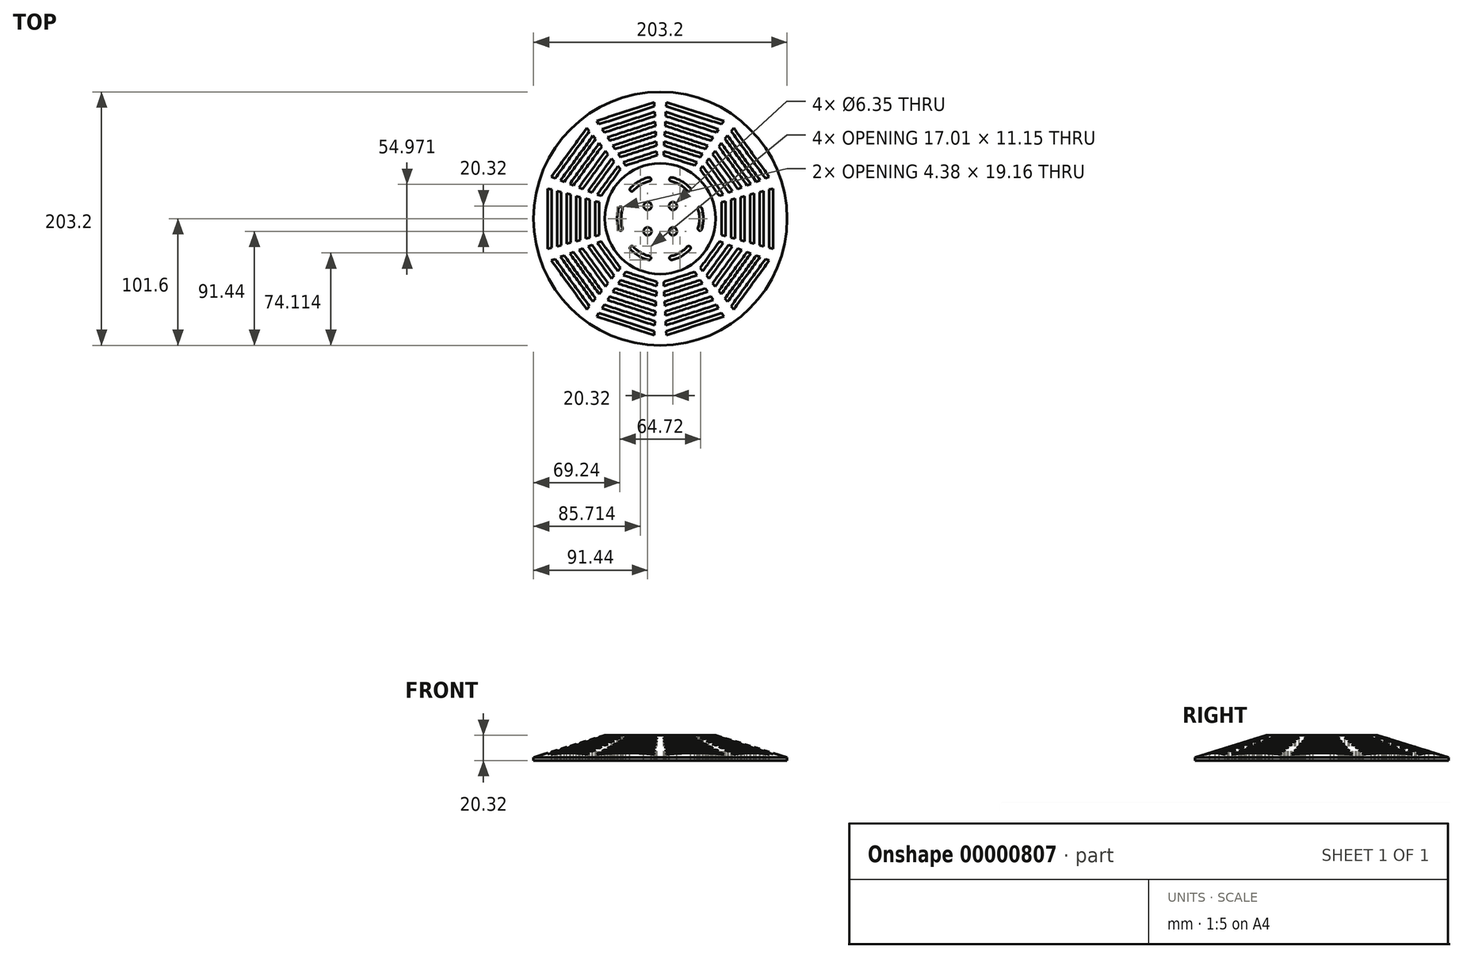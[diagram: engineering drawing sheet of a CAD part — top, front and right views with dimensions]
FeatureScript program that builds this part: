
annotation { "Feature Type Name" : "Feature", "Feature Type Description" : "" }
export const myFeature = defineFeature(function(context is Context, id is Id, definition is map)
    precondition{}
    {
        {
            var Q0;
            Q0=qCreatedBy(makeId("Front.planeOp"),FACE);
            var sketch = newSketch(context, id + "F0", { "sketchPlane" : qUnion([Q0])});
            skLineSegment(sketch, "E0", {"start": v(0, 0) * mm, "end": v(0, 20.32) * mm});
            skLineSegment(sketch, "E1", {"start": v(0, 20.32) * mm, "end": v(44.45, 20.32) * mm});
            skLineSegment(sketch, "E2", {"start": v(44.45, 20.32) * mm, "end": v(101.6, 2.54) * mm});
            skLineSegment(sketch, "E3", {"start": v(101.6, 2.54) * mm, "end": v(101.6, 0) * mm});
            skLineSegment(sketch, "E4", {"start": v(101.6, 0) * mm, "end": v(0, 0) * mm});
            skSolve(sketch);
        }
        {
            var Q0;
            Q0=makeQuery(id+"F0.imprint","IMPRINT",FACE,{"disambiguationData":[TD([[makeQuery(id+"F0.imprint","IMPRINT",EDGE,{"derivedFrom":sQuery(id+"F0.wireOp",EDGE,"E0")}),-1.0]])]});
            var Q1;
            Q1=sQuery(id+"F0.wireOp",EDGE,"E0");
            revolve(context, id + "F1", {"entities" : qUnion([Q0]), "axis" : qUnion([Q1]), "revolveType" : RevolveType.FULL});
        }
        {
            var Q0;
            Q0=makeQuery(id+"F1.opRevolve","SWEPT_FACE",FACE,{"disambiguationData":[OSD([sQuery(id+"F0.wireOp",EDGE,"E1")])]});
            var sketch = newSketch(context, id + "F2", { "sketchPlane" : qUnion([Q0])});
            skArc(sketch, "E5", {"start": v(-30.23, 7.53) * mm, "mid": v(-31.38, 0) * mm, "end": v(-30.23, -7.53) * mm});
            skArc(sketch, "E6.0", {"start": v(-33.27, 8.47) * mm, "mid": v(-34.55, 0) * mm, "end": v(-33.27, -8.47) * mm});
            skArc(sketch, "E7", {"start": v(-33.27, -8.47) * mm, "mid": v(-31.28, -9.52) * mm, "end": v(-30.23, -7.53) * mm});
            skArc(sketch, "E8", {"start": v(-30.23, 7.53) * mm, "mid": v(-31.28, 9.52) * mm, "end": v(-33.27, 8.47) * mm});
            skSolve(sketch);
        }
        {
            var Q0;
            Q0=makeQuery(id+"F2.imprint","IMPRINT",FACE,{"disambiguationData":[TD([[makeQuery(id+"F2.imprint","IMPRINT",EDGE,{"derivedFrom":sQuery(id+"F2.wireOp",EDGE,"E5")}),-1.0]])]});
            extrude(context, id + "F3", {"entities" : qUnion([Q0]), "endBound" : BoundingType.THROUGH_ALL, "oppositeDirection" : true, "depth" : 25.4 * mm});
        }
        {
            var Q0;
            Q0=makeQuery(id+"F3.opExtrude","SWEPT_BODY",BODY,{"disambiguationData":[OSD([sQuery(id+"F2.wireOp",EDGE,"E5"),sQuery(id+"F2.wireOp",EDGE,"E6.0"),sQuery(id+"F2.wireOp",EDGE,"E7"),sQuery(id+"F2.wireOp",EDGE,"E8")])]});
            var Q1;
            Q1=makeQuery(id+"F1.opRevolve","SWEPT_EDGE",EDGE,{"disambiguationData":[OSD([sQuery(id+"F0.wireOp",EDGE,"E2"),sQuery(id+"F0.wireOp",EDGE,"E3")])]});
            circularPattern(context, id + "F4", {"entities" : qUnion([Q0]), "axis" : qUnion([Q1]), "angle" : 360 * degree, "instanceCount" : 6, "equalSpace" : true});
        }
        {
            var Q0;
            Q0=makeQuery(id+"F3.opExtrude","SWEPT_BODY",BODY,{"disambiguationData":[OSD([sQuery(id+"F2.wireOp",EDGE,"E5"),sQuery(id+"F2.wireOp",EDGE,"E6.0"),sQuery(id+"F2.wireOp",EDGE,"E7"),sQuery(id+"F2.wireOp",EDGE,"E8")])]});
            var Q1;
            Q1=makeQuery(id+"F4.opPattern","COPY",BODY,{"derivedFrom":makeQuery(id+"F3.opExtrude","SWEPT_BODY",BODY,{"disambiguationData":[OSD([sQuery(id+"F2.wireOp",EDGE,"E5"),sQuery(id+"F2.wireOp",EDGE,"E6.0"),sQuery(id+"F2.wireOp",EDGE,"E7"),sQuery(id+"F2.wireOp",EDGE,"E8")])]}),"instanceName":"1"});
            var Q2;
            Q2=makeQuery(id+"F4.opPattern","COPY",BODY,{"derivedFrom":makeQuery(id+"F3.opExtrude","SWEPT_BODY",BODY,{"disambiguationData":[OSD([sQuery(id+"F2.wireOp",EDGE,"E5"),sQuery(id+"F2.wireOp",EDGE,"E6.0"),sQuery(id+"F2.wireOp",EDGE,"E7"),sQuery(id+"F2.wireOp",EDGE,"E8")])]}),"instanceName":"2"});
            var Q3;
            Q3=makeQuery(id+"F4.opPattern","COPY",BODY,{"derivedFrom":makeQuery(id+"F3.opExtrude","SWEPT_BODY",BODY,{"disambiguationData":[OSD([sQuery(id+"F2.wireOp",EDGE,"E5"),sQuery(id+"F2.wireOp",EDGE,"E6.0"),sQuery(id+"F2.wireOp",EDGE,"E7"),sQuery(id+"F2.wireOp",EDGE,"E8")])]}),"instanceName":"3"});
            var Q4;
            Q4=makeQuery(id+"F4.opPattern","COPY",BODY,{"derivedFrom":makeQuery(id+"F3.opExtrude","SWEPT_BODY",BODY,{"disambiguationData":[OSD([sQuery(id+"F2.wireOp",EDGE,"E5"),sQuery(id+"F2.wireOp",EDGE,"E6.0"),sQuery(id+"F2.wireOp",EDGE,"E7"),sQuery(id+"F2.wireOp",EDGE,"E8")])]}),"instanceName":"4"});
            var Q5;
            Q5=makeQuery(id+"F4.opPattern","COPY",BODY,{"derivedFrom":makeQuery(id+"F3.opExtrude","SWEPT_BODY",BODY,{"disambiguationData":[OSD([sQuery(id+"F2.wireOp",EDGE,"E5"),sQuery(id+"F2.wireOp",EDGE,"E6.0"),sQuery(id+"F2.wireOp",EDGE,"E7"),sQuery(id+"F2.wireOp",EDGE,"E8")])]}),"instanceName":"5"});
            var Q6;
            Q6=makeQuery(id+"F1.opRevolve","SWEPT_BODY",BODY,{"disambiguationData":[OSD([sQuery(id+"F0.wireOp",EDGE,"E0"),sQuery(id+"F0.wireOp",EDGE,"E1"),sQuery(id+"F0.wireOp",EDGE,"E2"),sQuery(id+"F0.wireOp",EDGE,"E3"),sQuery(id+"F0.wireOp",EDGE,"E4")])]});
            booleanBodies(context, id + "F5", {"operationType" : BooleanOperationType.SUBTRACTION, "tools" : qUnion([Q0, Q1, Q2, Q3, Q4, Q5]), "targets" : qUnion([Q6])});
        }
        {
            var Q0;
            Q0=makeQuery(id+"F1.opRevolve","SWEPT_FACE",FACE,{"disambiguationData":[OSD([sQuery(id+"F0.wireOp",EDGE,"E1")])]});
            var sketch = newSketch(context, id + "F6", { "sketchPlane" : qUnion([Q0])});
            skLineSegment(sketch, "E9", {"start": v(0, 0) * mm, "end": v(-98.14, 26.3) * mm});
            skLineSegment(sketch, "E10", {"start": v(0, 0) * mm, "end": v(-98.14, -26.3) * mm});
            skLineSegment(sketch, "E11", {"start": v(-49.07, -13.15) * mm, "end": v(-49.07, 13.15) * mm});
            skLineSegment(sketch, "E12", {"start": v(-52.24, -14) * mm, "end": v(-52.24, 14) * mm});
            skLineSegment(sketch, "E13", {"start": v(-56.69, -15.19) * mm, "end": v(-56.69, 15.19) * mm});
            skLineSegment(sketch, "E14", {"start": v(-59.86, -16.04) * mm, "end": v(-59.86, 16.04) * mm});
            skLineSegment(sketch, "E15", {"start": v(-64.3, -17.23) * mm, "end": v(-64.3, 17.23) * mm});
            skLineSegment(sketch, "E16", {"start": v(-67.48, -18.08) * mm, "end": v(-67.48, 18.08) * mm});
            skLineSegment(sketch, "E17", {"start": v(-71.93, -19.27) * mm, "end": v(-71.93, 19.27) * mm});
            skLineSegment(sketch, "E18", {"start": v(-75.1, -20.12) * mm, "end": v(-75.1, 20.12) * mm});
            skLineSegment(sketch, "E19", {"start": v(-79.55, -21.32) * mm, "end": v(-79.55, 21.32) * mm});
            skLineSegment(sketch, "E20", {"start": v(-82.72, -22.17) * mm, "end": v(-82.72, 22.17) * mm});
            skLineSegment(sketch, "E21", {"start": v(-87.17, -23.36) * mm, "end": v(-87.17, 23.36) * mm});
            skLineSegment(sketch, "E22", {"start": v(-90.34, -24.2) * mm, "end": v(-90.34, 24.2) * mm});
            skSolve(sketch);
        }
        {
            var Q0;
            {var subQ1=sQuery(id+"F6.wireOp",EDGE,"E19");Q0=makeQuery(id+"F6.imprint","IMPRINT",FACE,{"disambiguationData":[TD([[makeQuery(id+"F6.imprint","IMPRINT",EDGE,{"derivedFrom":subQ1}),1.0]])]});}
            var Q1;
            {var subQ1=sQuery(id+"F6.wireOp",EDGE,"E17");Q1=makeQuery(id+"F6.imprint","IMPRINT",FACE,{"disambiguationData":[TD([[makeQuery(id+"F6.imprint","IMPRINT",EDGE,{"derivedFrom":subQ1}),1.0]])]});}
            var Q2;
            {var subQ1=sQuery(id+"F6.wireOp",EDGE,"E15");Q2=makeQuery(id+"F6.imprint","IMPRINT",FACE,{"disambiguationData":[TD([[makeQuery(id+"F6.imprint","IMPRINT",EDGE,{"derivedFrom":subQ1}),1.0]])]});}
            var Q3;
            {var subQ1=sQuery(id+"F6.wireOp",EDGE,"E13");Q3=makeQuery(id+"F6.imprint","IMPRINT",FACE,{"disambiguationData":[TD([[makeQuery(id+"F6.imprint","IMPRINT",EDGE,{"derivedFrom":subQ1}),1.0]])]});}
            var Q4;
            {var subQ1=sQuery(id+"F6.wireOp",EDGE,"E11");Q4=makeQuery(id+"F6.imprint","IMPRINT",FACE,{"disambiguationData":[TD([[makeQuery(id+"F6.imprint","IMPRINT",EDGE,{"derivedFrom":subQ1}),1.0]])]});}
            var Q5;
            {var subQ1=sQuery(id+"F6.wireOp",EDGE,"E21");Q5=makeQuery(id+"F6.imprint","IMPRINT",FACE,{"disambiguationData":[TD([[makeQuery(id+"F6.imprint","IMPRINT",EDGE,{"derivedFrom":subQ1}),1.0]])]});}
            extrude(context, id + "F7", {"entities" : qUnion([Q0, Q1, Q2, Q3, Q4, Q5]), "oppositeDirection" : true, "depth" : 25.4 * mm});
        }
        {
            var Q0;
            Q0=makeQuery(id+"F7.opExtrude","SWEPT_BODY",BODY,{"disambiguationData":[OSD([sQuery(id+"F6.wireOp",EDGE,"E9"),sQuery(id+"F6.wireOp",EDGE,"E10"),sQuery(id+"F6.wireOp",EDGE,"E21"),sQuery(id+"F6.wireOp",EDGE,"E22")])]});
            var Q1;
            Q1=makeQuery(id+"F7.opExtrude","SWEPT_BODY",BODY,{"disambiguationData":[OSD([sQuery(id+"F6.wireOp",EDGE,"E9"),sQuery(id+"F6.wireOp",EDGE,"E10"),sQuery(id+"F6.wireOp",EDGE,"E19"),sQuery(id+"F6.wireOp",EDGE,"E20")])]});
            var Q2;
            Q2=makeQuery(id+"F7.opExtrude","SWEPT_BODY",BODY,{"disambiguationData":[OSD([sQuery(id+"F6.wireOp",EDGE,"E9"),sQuery(id+"F6.wireOp",EDGE,"E10"),sQuery(id+"F6.wireOp",EDGE,"E17"),sQuery(id+"F6.wireOp",EDGE,"E18")])]});
            var Q3;
            Q3=makeQuery(id+"F7.opExtrude","SWEPT_BODY",BODY,{"disambiguationData":[OSD([sQuery(id+"F6.wireOp",EDGE,"E9"),sQuery(id+"F6.wireOp",EDGE,"E10"),sQuery(id+"F6.wireOp",EDGE,"E15"),sQuery(id+"F6.wireOp",EDGE,"E16")])]});
            var Q4;
            Q4=makeQuery(id+"F7.opExtrude","SWEPT_BODY",BODY,{"disambiguationData":[OSD([sQuery(id+"F6.wireOp",EDGE,"E9"),sQuery(id+"F6.wireOp",EDGE,"E10"),sQuery(id+"F6.wireOp",EDGE,"E13"),sQuery(id+"F6.wireOp",EDGE,"E14")])]});
            var Q5;
            Q5=makeQuery(id+"F7.opExtrude","SWEPT_BODY",BODY,{"disambiguationData":[OSD([sQuery(id+"F6.wireOp",EDGE,"E9"),sQuery(id+"F6.wireOp",EDGE,"E10"),sQuery(id+"F6.wireOp",EDGE,"E11"),sQuery(id+"F6.wireOp",EDGE,"E12")])]});
            var Q6;
            Q6=makeQuery(id+"F1.opRevolve","SWEPT_EDGE",EDGE,{"disambiguationData":[OSD([sQuery(id+"F0.wireOp",EDGE,"E2"),sQuery(id+"F0.wireOp",EDGE,"E3")])]});
            circularPattern(context, id + "F8", {"entities" : qUnion([Q0, Q1, Q2, Q3, Q4, Q5]), "axis" : qUnion([Q6]), "angle" : 360 * degree, "instanceCount" : 10, "equalSpace" : true});
        }
        {
            var Q0;
            Q0=makeQuery(id+"F7.opExtrude","SWEPT_BODY",BODY,{"disambiguationData":[OSD([sQuery(id+"F6.wireOp",EDGE,"E9"),sQuery(id+"F6.wireOp",EDGE,"E10"),sQuery(id+"F6.wireOp",EDGE,"E21"),sQuery(id+"F6.wireOp",EDGE,"E22")])]});
            var Q1;
            Q1=makeQuery(id+"F7.opExtrude","SWEPT_BODY",BODY,{"disambiguationData":[OSD([sQuery(id+"F6.wireOp",EDGE,"E9"),sQuery(id+"F6.wireOp",EDGE,"E10"),sQuery(id+"F6.wireOp",EDGE,"E11"),sQuery(id+"F6.wireOp",EDGE,"E12")])]});
            var Q2;
            Q2=makeQuery(id+"F7.opExtrude","SWEPT_BODY",BODY,{"disambiguationData":[OSD([sQuery(id+"F6.wireOp",EDGE,"E9"),sQuery(id+"F6.wireOp",EDGE,"E10"),sQuery(id+"F6.wireOp",EDGE,"E13"),sQuery(id+"F6.wireOp",EDGE,"E14")])]});
            var Q3;
            Q3=makeQuery(id+"F7.opExtrude","SWEPT_BODY",BODY,{"disambiguationData":[OSD([sQuery(id+"F6.wireOp",EDGE,"E9"),sQuery(id+"F6.wireOp",EDGE,"E10"),sQuery(id+"F6.wireOp",EDGE,"E15"),sQuery(id+"F6.wireOp",EDGE,"E16")])]});
            var Q4;
            Q4=makeQuery(id+"F7.opExtrude","SWEPT_BODY",BODY,{"disambiguationData":[OSD([sQuery(id+"F6.wireOp",EDGE,"E9"),sQuery(id+"F6.wireOp",EDGE,"E10"),sQuery(id+"F6.wireOp",EDGE,"E17"),sQuery(id+"F6.wireOp",EDGE,"E18")])]});
            var Q5;
            Q5=makeQuery(id+"F7.opExtrude","SWEPT_BODY",BODY,{"disambiguationData":[OSD([sQuery(id+"F6.wireOp",EDGE,"E9"),sQuery(id+"F6.wireOp",EDGE,"E10"),sQuery(id+"F6.wireOp",EDGE,"E19"),sQuery(id+"F6.wireOp",EDGE,"E20")])]});
            var Q6;
            Q6=makeQuery(id+"F8.opPattern","COPY",BODY,{"derivedFrom":makeQuery(id+"F7.opExtrude","SWEPT_BODY",BODY,{"disambiguationData":[OSD([sQuery(id+"F6.wireOp",EDGE,"E9"),sQuery(id+"F6.wireOp",EDGE,"E10"),sQuery(id+"F6.wireOp",EDGE,"E21"),sQuery(id+"F6.wireOp",EDGE,"E22")])]}),"instanceName":"1"});
            var Q7;
            Q7=makeQuery(id+"F8.opPattern","COPY",BODY,{"derivedFrom":makeQuery(id+"F7.opExtrude","SWEPT_BODY",BODY,{"disambiguationData":[OSD([sQuery(id+"F6.wireOp",EDGE,"E9"),sQuery(id+"F6.wireOp",EDGE,"E10"),sQuery(id+"F6.wireOp",EDGE,"E11"),sQuery(id+"F6.wireOp",EDGE,"E12")])]}),"instanceName":"1"});
            var Q8;
            Q8=makeQuery(id+"F8.opPattern","COPY",BODY,{"derivedFrom":makeQuery(id+"F7.opExtrude","SWEPT_BODY",BODY,{"disambiguationData":[OSD([sQuery(id+"F6.wireOp",EDGE,"E9"),sQuery(id+"F6.wireOp",EDGE,"E10"),sQuery(id+"F6.wireOp",EDGE,"E13"),sQuery(id+"F6.wireOp",EDGE,"E14")])]}),"instanceName":"1"});
            var Q9;
            Q9=makeQuery(id+"F8.opPattern","COPY",BODY,{"derivedFrom":makeQuery(id+"F7.opExtrude","SWEPT_BODY",BODY,{"disambiguationData":[OSD([sQuery(id+"F6.wireOp",EDGE,"E9"),sQuery(id+"F6.wireOp",EDGE,"E10"),sQuery(id+"F6.wireOp",EDGE,"E15"),sQuery(id+"F6.wireOp",EDGE,"E16")])]}),"instanceName":"1"});
            var Q10;
            Q10=makeQuery(id+"F8.opPattern","COPY",BODY,{"derivedFrom":makeQuery(id+"F7.opExtrude","SWEPT_BODY",BODY,{"disambiguationData":[OSD([sQuery(id+"F6.wireOp",EDGE,"E9"),sQuery(id+"F6.wireOp",EDGE,"E10"),sQuery(id+"F6.wireOp",EDGE,"E17"),sQuery(id+"F6.wireOp",EDGE,"E18")])]}),"instanceName":"1"});
            var Q11;
            Q11=makeQuery(id+"F8.opPattern","COPY",BODY,{"derivedFrom":makeQuery(id+"F7.opExtrude","SWEPT_BODY",BODY,{"disambiguationData":[OSD([sQuery(id+"F6.wireOp",EDGE,"E9"),sQuery(id+"F6.wireOp",EDGE,"E10"),sQuery(id+"F6.wireOp",EDGE,"E19"),sQuery(id+"F6.wireOp",EDGE,"E20")])]}),"instanceName":"1"});
            var Q12;
            Q12=makeQuery(id+"F8.opPattern","COPY",BODY,{"derivedFrom":makeQuery(id+"F7.opExtrude","SWEPT_BODY",BODY,{"disambiguationData":[OSD([sQuery(id+"F6.wireOp",EDGE,"E9"),sQuery(id+"F6.wireOp",EDGE,"E10"),sQuery(id+"F6.wireOp",EDGE,"E21"),sQuery(id+"F6.wireOp",EDGE,"E22")])]}),"instanceName":"2"});
            var Q13;
            Q13=makeQuery(id+"F8.opPattern","COPY",BODY,{"derivedFrom":makeQuery(id+"F7.opExtrude","SWEPT_BODY",BODY,{"disambiguationData":[OSD([sQuery(id+"F6.wireOp",EDGE,"E9"),sQuery(id+"F6.wireOp",EDGE,"E10"),sQuery(id+"F6.wireOp",EDGE,"E11"),sQuery(id+"F6.wireOp",EDGE,"E12")])]}),"instanceName":"2"});
            var Q14;
            Q14=makeQuery(id+"F8.opPattern","COPY",BODY,{"derivedFrom":makeQuery(id+"F7.opExtrude","SWEPT_BODY",BODY,{"disambiguationData":[OSD([sQuery(id+"F6.wireOp",EDGE,"E9"),sQuery(id+"F6.wireOp",EDGE,"E10"),sQuery(id+"F6.wireOp",EDGE,"E13"),sQuery(id+"F6.wireOp",EDGE,"E14")])]}),"instanceName":"2"});
            var Q15;
            Q15=makeQuery(id+"F8.opPattern","COPY",BODY,{"derivedFrom":makeQuery(id+"F7.opExtrude","SWEPT_BODY",BODY,{"disambiguationData":[OSD([sQuery(id+"F6.wireOp",EDGE,"E9"),sQuery(id+"F6.wireOp",EDGE,"E10"),sQuery(id+"F6.wireOp",EDGE,"E15"),sQuery(id+"F6.wireOp",EDGE,"E16")])]}),"instanceName":"2"});
            var Q16;
            Q16=makeQuery(id+"F8.opPattern","COPY",BODY,{"derivedFrom":makeQuery(id+"F7.opExtrude","SWEPT_BODY",BODY,{"disambiguationData":[OSD([sQuery(id+"F6.wireOp",EDGE,"E9"),sQuery(id+"F6.wireOp",EDGE,"E10"),sQuery(id+"F6.wireOp",EDGE,"E17"),sQuery(id+"F6.wireOp",EDGE,"E18")])]}),"instanceName":"2"});
            var Q17;
            Q17=makeQuery(id+"F8.opPattern","COPY",BODY,{"derivedFrom":makeQuery(id+"F7.opExtrude","SWEPT_BODY",BODY,{"disambiguationData":[OSD([sQuery(id+"F6.wireOp",EDGE,"E9"),sQuery(id+"F6.wireOp",EDGE,"E10"),sQuery(id+"F6.wireOp",EDGE,"E19"),sQuery(id+"F6.wireOp",EDGE,"E20")])]}),"instanceName":"2"});
            var Q18;
            Q18=makeQuery(id+"F8.opPattern","COPY",BODY,{"derivedFrom":makeQuery(id+"F7.opExtrude","SWEPT_BODY",BODY,{"disambiguationData":[OSD([sQuery(id+"F6.wireOp",EDGE,"E9"),sQuery(id+"F6.wireOp",EDGE,"E10"),sQuery(id+"F6.wireOp",EDGE,"E21"),sQuery(id+"F6.wireOp",EDGE,"E22")])]}),"instanceName":"3"});
            var Q19;
            Q19=makeQuery(id+"F8.opPattern","COPY",BODY,{"derivedFrom":makeQuery(id+"F7.opExtrude","SWEPT_BODY",BODY,{"disambiguationData":[OSD([sQuery(id+"F6.wireOp",EDGE,"E9"),sQuery(id+"F6.wireOp",EDGE,"E10"),sQuery(id+"F6.wireOp",EDGE,"E11"),sQuery(id+"F6.wireOp",EDGE,"E12")])]}),"instanceName":"3"});
            var Q20;
            Q20=makeQuery(id+"F8.opPattern","COPY",BODY,{"derivedFrom":makeQuery(id+"F7.opExtrude","SWEPT_BODY",BODY,{"disambiguationData":[OSD([sQuery(id+"F6.wireOp",EDGE,"E9"),sQuery(id+"F6.wireOp",EDGE,"E10"),sQuery(id+"F6.wireOp",EDGE,"E13"),sQuery(id+"F6.wireOp",EDGE,"E14")])]}),"instanceName":"3"});
            var Q21;
            Q21=makeQuery(id+"F8.opPattern","COPY",BODY,{"derivedFrom":makeQuery(id+"F7.opExtrude","SWEPT_BODY",BODY,{"disambiguationData":[OSD([sQuery(id+"F6.wireOp",EDGE,"E9"),sQuery(id+"F6.wireOp",EDGE,"E10"),sQuery(id+"F6.wireOp",EDGE,"E15"),sQuery(id+"F6.wireOp",EDGE,"E16")])]}),"instanceName":"3"});
            var Q22;
            Q22=makeQuery(id+"F8.opPattern","COPY",BODY,{"derivedFrom":makeQuery(id+"F7.opExtrude","SWEPT_BODY",BODY,{"disambiguationData":[OSD([sQuery(id+"F6.wireOp",EDGE,"E9"),sQuery(id+"F6.wireOp",EDGE,"E10"),sQuery(id+"F6.wireOp",EDGE,"E17"),sQuery(id+"F6.wireOp",EDGE,"E18")])]}),"instanceName":"3"});
            var Q23;
            Q23=makeQuery(id+"F8.opPattern","COPY",BODY,{"derivedFrom":makeQuery(id+"F7.opExtrude","SWEPT_BODY",BODY,{"disambiguationData":[OSD([sQuery(id+"F6.wireOp",EDGE,"E9"),sQuery(id+"F6.wireOp",EDGE,"E10"),sQuery(id+"F6.wireOp",EDGE,"E19"),sQuery(id+"F6.wireOp",EDGE,"E20")])]}),"instanceName":"3"});
            var Q24;
            Q24=makeQuery(id+"F8.opPattern","COPY",BODY,{"derivedFrom":makeQuery(id+"F7.opExtrude","SWEPT_BODY",BODY,{"disambiguationData":[OSD([sQuery(id+"F6.wireOp",EDGE,"E9"),sQuery(id+"F6.wireOp",EDGE,"E10"),sQuery(id+"F6.wireOp",EDGE,"E21"),sQuery(id+"F6.wireOp",EDGE,"E22")])]}),"instanceName":"4"});
            var Q25;
            Q25=makeQuery(id+"F8.opPattern","COPY",BODY,{"derivedFrom":makeQuery(id+"F7.opExtrude","SWEPT_BODY",BODY,{"disambiguationData":[OSD([sQuery(id+"F6.wireOp",EDGE,"E9"),sQuery(id+"F6.wireOp",EDGE,"E10"),sQuery(id+"F6.wireOp",EDGE,"E11"),sQuery(id+"F6.wireOp",EDGE,"E12")])]}),"instanceName":"4"});
            var Q26;
            Q26=makeQuery(id+"F8.opPattern","COPY",BODY,{"derivedFrom":makeQuery(id+"F7.opExtrude","SWEPT_BODY",BODY,{"disambiguationData":[OSD([sQuery(id+"F6.wireOp",EDGE,"E9"),sQuery(id+"F6.wireOp",EDGE,"E10"),sQuery(id+"F6.wireOp",EDGE,"E13"),sQuery(id+"F6.wireOp",EDGE,"E14")])]}),"instanceName":"4"});
            var Q27;
            Q27=makeQuery(id+"F8.opPattern","COPY",BODY,{"derivedFrom":makeQuery(id+"F7.opExtrude","SWEPT_BODY",BODY,{"disambiguationData":[OSD([sQuery(id+"F6.wireOp",EDGE,"E9"),sQuery(id+"F6.wireOp",EDGE,"E10"),sQuery(id+"F6.wireOp",EDGE,"E15"),sQuery(id+"F6.wireOp",EDGE,"E16")])]}),"instanceName":"4"});
            var Q28;
            Q28=makeQuery(id+"F8.opPattern","COPY",BODY,{"derivedFrom":makeQuery(id+"F7.opExtrude","SWEPT_BODY",BODY,{"disambiguationData":[OSD([sQuery(id+"F6.wireOp",EDGE,"E9"),sQuery(id+"F6.wireOp",EDGE,"E10"),sQuery(id+"F6.wireOp",EDGE,"E17"),sQuery(id+"F6.wireOp",EDGE,"E18")])]}),"instanceName":"4"});
            var Q29;
            Q29=makeQuery(id+"F8.opPattern","COPY",BODY,{"derivedFrom":makeQuery(id+"F7.opExtrude","SWEPT_BODY",BODY,{"disambiguationData":[OSD([sQuery(id+"F6.wireOp",EDGE,"E9"),sQuery(id+"F6.wireOp",EDGE,"E10"),sQuery(id+"F6.wireOp",EDGE,"E19"),sQuery(id+"F6.wireOp",EDGE,"E20")])]}),"instanceName":"4"});
            var Q30;
            Q30=makeQuery(id+"F8.opPattern","COPY",BODY,{"derivedFrom":makeQuery(id+"F7.opExtrude","SWEPT_BODY",BODY,{"disambiguationData":[OSD([sQuery(id+"F6.wireOp",EDGE,"E9"),sQuery(id+"F6.wireOp",EDGE,"E10"),sQuery(id+"F6.wireOp",EDGE,"E21"),sQuery(id+"F6.wireOp",EDGE,"E22")])]}),"instanceName":"5"});
            var Q31;
            Q31=makeQuery(id+"F8.opPattern","COPY",BODY,{"derivedFrom":makeQuery(id+"F7.opExtrude","SWEPT_BODY",BODY,{"disambiguationData":[OSD([sQuery(id+"F6.wireOp",EDGE,"E9"),sQuery(id+"F6.wireOp",EDGE,"E10"),sQuery(id+"F6.wireOp",EDGE,"E11"),sQuery(id+"F6.wireOp",EDGE,"E12")])]}),"instanceName":"5"});
            var Q32;
            Q32=makeQuery(id+"F8.opPattern","COPY",BODY,{"derivedFrom":makeQuery(id+"F7.opExtrude","SWEPT_BODY",BODY,{"disambiguationData":[OSD([sQuery(id+"F6.wireOp",EDGE,"E9"),sQuery(id+"F6.wireOp",EDGE,"E10"),sQuery(id+"F6.wireOp",EDGE,"E13"),sQuery(id+"F6.wireOp",EDGE,"E14")])]}),"instanceName":"5"});
            var Q33;
            Q33=makeQuery(id+"F8.opPattern","COPY",BODY,{"derivedFrom":makeQuery(id+"F7.opExtrude","SWEPT_BODY",BODY,{"disambiguationData":[OSD([sQuery(id+"F6.wireOp",EDGE,"E9"),sQuery(id+"F6.wireOp",EDGE,"E10"),sQuery(id+"F6.wireOp",EDGE,"E15"),sQuery(id+"F6.wireOp",EDGE,"E16")])]}),"instanceName":"5"});
            var Q34;
            Q34=makeQuery(id+"F8.opPattern","COPY",BODY,{"derivedFrom":makeQuery(id+"F7.opExtrude","SWEPT_BODY",BODY,{"disambiguationData":[OSD([sQuery(id+"F6.wireOp",EDGE,"E9"),sQuery(id+"F6.wireOp",EDGE,"E10"),sQuery(id+"F6.wireOp",EDGE,"E17"),sQuery(id+"F6.wireOp",EDGE,"E18")])]}),"instanceName":"5"});
            var Q35;
            Q35=makeQuery(id+"F8.opPattern","COPY",BODY,{"derivedFrom":makeQuery(id+"F7.opExtrude","SWEPT_BODY",BODY,{"disambiguationData":[OSD([sQuery(id+"F6.wireOp",EDGE,"E9"),sQuery(id+"F6.wireOp",EDGE,"E10"),sQuery(id+"F6.wireOp",EDGE,"E19"),sQuery(id+"F6.wireOp",EDGE,"E20")])]}),"instanceName":"5"});
            var Q36;
            Q36=makeQuery(id+"F8.opPattern","COPY",BODY,{"derivedFrom":makeQuery(id+"F7.opExtrude","SWEPT_BODY",BODY,{"disambiguationData":[OSD([sQuery(id+"F6.wireOp",EDGE,"E9"),sQuery(id+"F6.wireOp",EDGE,"E10"),sQuery(id+"F6.wireOp",EDGE,"E21"),sQuery(id+"F6.wireOp",EDGE,"E22")])]}),"instanceName":"6"});
            var Q37;
            Q37=makeQuery(id+"F8.opPattern","COPY",BODY,{"derivedFrom":makeQuery(id+"F7.opExtrude","SWEPT_BODY",BODY,{"disambiguationData":[OSD([sQuery(id+"F6.wireOp",EDGE,"E9"),sQuery(id+"F6.wireOp",EDGE,"E10"),sQuery(id+"F6.wireOp",EDGE,"E11"),sQuery(id+"F6.wireOp",EDGE,"E12")])]}),"instanceName":"6"});
            var Q38;
            Q38=makeQuery(id+"F8.opPattern","COPY",BODY,{"derivedFrom":makeQuery(id+"F7.opExtrude","SWEPT_BODY",BODY,{"disambiguationData":[OSD([sQuery(id+"F6.wireOp",EDGE,"E9"),sQuery(id+"F6.wireOp",EDGE,"E10"),sQuery(id+"F6.wireOp",EDGE,"E13"),sQuery(id+"F6.wireOp",EDGE,"E14")])]}),"instanceName":"6"});
            var Q39;
            Q39=makeQuery(id+"F8.opPattern","COPY",BODY,{"derivedFrom":makeQuery(id+"F7.opExtrude","SWEPT_BODY",BODY,{"disambiguationData":[OSD([sQuery(id+"F6.wireOp",EDGE,"E9"),sQuery(id+"F6.wireOp",EDGE,"E10"),sQuery(id+"F6.wireOp",EDGE,"E15"),sQuery(id+"F6.wireOp",EDGE,"E16")])]}),"instanceName":"6"});
            var Q40;
            Q40=makeQuery(id+"F8.opPattern","COPY",BODY,{"derivedFrom":makeQuery(id+"F7.opExtrude","SWEPT_BODY",BODY,{"disambiguationData":[OSD([sQuery(id+"F6.wireOp",EDGE,"E9"),sQuery(id+"F6.wireOp",EDGE,"E10"),sQuery(id+"F6.wireOp",EDGE,"E17"),sQuery(id+"F6.wireOp",EDGE,"E18")])]}),"instanceName":"6"});
            var Q41;
            Q41=makeQuery(id+"F8.opPattern","COPY",BODY,{"derivedFrom":makeQuery(id+"F7.opExtrude","SWEPT_BODY",BODY,{"disambiguationData":[OSD([sQuery(id+"F6.wireOp",EDGE,"E9"),sQuery(id+"F6.wireOp",EDGE,"E10"),sQuery(id+"F6.wireOp",EDGE,"E19"),sQuery(id+"F6.wireOp",EDGE,"E20")])]}),"instanceName":"6"});
            var Q42;
            Q42=makeQuery(id+"F8.opPattern","COPY",BODY,{"derivedFrom":makeQuery(id+"F7.opExtrude","SWEPT_BODY",BODY,{"disambiguationData":[OSD([sQuery(id+"F6.wireOp",EDGE,"E9"),sQuery(id+"F6.wireOp",EDGE,"E10"),sQuery(id+"F6.wireOp",EDGE,"E21"),sQuery(id+"F6.wireOp",EDGE,"E22")])]}),"instanceName":"7"});
            var Q43;
            Q43=makeQuery(id+"F8.opPattern","COPY",BODY,{"derivedFrom":makeQuery(id+"F7.opExtrude","SWEPT_BODY",BODY,{"disambiguationData":[OSD([sQuery(id+"F6.wireOp",EDGE,"E9"),sQuery(id+"F6.wireOp",EDGE,"E10"),sQuery(id+"F6.wireOp",EDGE,"E11"),sQuery(id+"F6.wireOp",EDGE,"E12")])]}),"instanceName":"7"});
            var Q44;
            Q44=makeQuery(id+"F8.opPattern","COPY",BODY,{"derivedFrom":makeQuery(id+"F7.opExtrude","SWEPT_BODY",BODY,{"disambiguationData":[OSD([sQuery(id+"F6.wireOp",EDGE,"E9"),sQuery(id+"F6.wireOp",EDGE,"E10"),sQuery(id+"F6.wireOp",EDGE,"E13"),sQuery(id+"F6.wireOp",EDGE,"E14")])]}),"instanceName":"7"});
            var Q45;
            Q45=makeQuery(id+"F8.opPattern","COPY",BODY,{"derivedFrom":makeQuery(id+"F7.opExtrude","SWEPT_BODY",BODY,{"disambiguationData":[OSD([sQuery(id+"F6.wireOp",EDGE,"E9"),sQuery(id+"F6.wireOp",EDGE,"E10"),sQuery(id+"F6.wireOp",EDGE,"E15"),sQuery(id+"F6.wireOp",EDGE,"E16")])]}),"instanceName":"7"});
            var Q46;
            Q46=makeQuery(id+"F8.opPattern","COPY",BODY,{"derivedFrom":makeQuery(id+"F7.opExtrude","SWEPT_BODY",BODY,{"disambiguationData":[OSD([sQuery(id+"F6.wireOp",EDGE,"E9"),sQuery(id+"F6.wireOp",EDGE,"E10"),sQuery(id+"F6.wireOp",EDGE,"E17"),sQuery(id+"F6.wireOp",EDGE,"E18")])]}),"instanceName":"7"});
            var Q47;
            Q47=makeQuery(id+"F8.opPattern","COPY",BODY,{"derivedFrom":makeQuery(id+"F7.opExtrude","SWEPT_BODY",BODY,{"disambiguationData":[OSD([sQuery(id+"F6.wireOp",EDGE,"E9"),sQuery(id+"F6.wireOp",EDGE,"E10"),sQuery(id+"F6.wireOp",EDGE,"E19"),sQuery(id+"F6.wireOp",EDGE,"E20")])]}),"instanceName":"7"});
            var Q48;
            Q48=makeQuery(id+"F8.opPattern","COPY",BODY,{"derivedFrom":makeQuery(id+"F7.opExtrude","SWEPT_BODY",BODY,{"disambiguationData":[OSD([sQuery(id+"F6.wireOp",EDGE,"E9"),sQuery(id+"F6.wireOp",EDGE,"E10"),sQuery(id+"F6.wireOp",EDGE,"E21"),sQuery(id+"F6.wireOp",EDGE,"E22")])]}),"instanceName":"8"});
            var Q49;
            Q49=makeQuery(id+"F8.opPattern","COPY",BODY,{"derivedFrom":makeQuery(id+"F7.opExtrude","SWEPT_BODY",BODY,{"disambiguationData":[OSD([sQuery(id+"F6.wireOp",EDGE,"E9"),sQuery(id+"F6.wireOp",EDGE,"E10"),sQuery(id+"F6.wireOp",EDGE,"E11"),sQuery(id+"F6.wireOp",EDGE,"E12")])]}),"instanceName":"8"});
            var Q50;
            Q50=makeQuery(id+"F8.opPattern","COPY",BODY,{"derivedFrom":makeQuery(id+"F7.opExtrude","SWEPT_BODY",BODY,{"disambiguationData":[OSD([sQuery(id+"F6.wireOp",EDGE,"E9"),sQuery(id+"F6.wireOp",EDGE,"E10"),sQuery(id+"F6.wireOp",EDGE,"E13"),sQuery(id+"F6.wireOp",EDGE,"E14")])]}),"instanceName":"8"});
            var Q51;
            Q51=makeQuery(id+"F8.opPattern","COPY",BODY,{"derivedFrom":makeQuery(id+"F7.opExtrude","SWEPT_BODY",BODY,{"disambiguationData":[OSD([sQuery(id+"F6.wireOp",EDGE,"E9"),sQuery(id+"F6.wireOp",EDGE,"E10"),sQuery(id+"F6.wireOp",EDGE,"E15"),sQuery(id+"F6.wireOp",EDGE,"E16")])]}),"instanceName":"8"});
            var Q52;
            Q52=makeQuery(id+"F8.opPattern","COPY",BODY,{"derivedFrom":makeQuery(id+"F7.opExtrude","SWEPT_BODY",BODY,{"disambiguationData":[OSD([sQuery(id+"F6.wireOp",EDGE,"E9"),sQuery(id+"F6.wireOp",EDGE,"E10"),sQuery(id+"F6.wireOp",EDGE,"E17"),sQuery(id+"F6.wireOp",EDGE,"E18")])]}),"instanceName":"8"});
            var Q53;
            Q53=makeQuery(id+"F8.opPattern","COPY",BODY,{"derivedFrom":makeQuery(id+"F7.opExtrude","SWEPT_BODY",BODY,{"disambiguationData":[OSD([sQuery(id+"F6.wireOp",EDGE,"E9"),sQuery(id+"F6.wireOp",EDGE,"E10"),sQuery(id+"F6.wireOp",EDGE,"E19"),sQuery(id+"F6.wireOp",EDGE,"E20")])]}),"instanceName":"8"});
            var Q54;
            Q54=makeQuery(id+"F8.opPattern","COPY",BODY,{"derivedFrom":makeQuery(id+"F7.opExtrude","SWEPT_BODY",BODY,{"disambiguationData":[OSD([sQuery(id+"F6.wireOp",EDGE,"E9"),sQuery(id+"F6.wireOp",EDGE,"E10"),sQuery(id+"F6.wireOp",EDGE,"E21"),sQuery(id+"F6.wireOp",EDGE,"E22")])]}),"instanceName":"9"});
            var Q55;
            Q55=makeQuery(id+"F8.opPattern","COPY",BODY,{"derivedFrom":makeQuery(id+"F7.opExtrude","SWEPT_BODY",BODY,{"disambiguationData":[OSD([sQuery(id+"F6.wireOp",EDGE,"E9"),sQuery(id+"F6.wireOp",EDGE,"E10"),sQuery(id+"F6.wireOp",EDGE,"E11"),sQuery(id+"F6.wireOp",EDGE,"E12")])]}),"instanceName":"9"});
            var Q56;
            Q56=makeQuery(id+"F8.opPattern","COPY",BODY,{"derivedFrom":makeQuery(id+"F7.opExtrude","SWEPT_BODY",BODY,{"disambiguationData":[OSD([sQuery(id+"F6.wireOp",EDGE,"E9"),sQuery(id+"F6.wireOp",EDGE,"E10"),sQuery(id+"F6.wireOp",EDGE,"E13"),sQuery(id+"F6.wireOp",EDGE,"E14")])]}),"instanceName":"9"});
            var Q57;
            Q57=makeQuery(id+"F8.opPattern","COPY",BODY,{"derivedFrom":makeQuery(id+"F7.opExtrude","SWEPT_BODY",BODY,{"disambiguationData":[OSD([sQuery(id+"F6.wireOp",EDGE,"E9"),sQuery(id+"F6.wireOp",EDGE,"E10"),sQuery(id+"F6.wireOp",EDGE,"E15"),sQuery(id+"F6.wireOp",EDGE,"E16")])]}),"instanceName":"9"});
            var Q58;
            Q58=makeQuery(id+"F8.opPattern","COPY",BODY,{"derivedFrom":makeQuery(id+"F7.opExtrude","SWEPT_BODY",BODY,{"disambiguationData":[OSD([sQuery(id+"F6.wireOp",EDGE,"E9"),sQuery(id+"F6.wireOp",EDGE,"E10"),sQuery(id+"F6.wireOp",EDGE,"E17"),sQuery(id+"F6.wireOp",EDGE,"E18")])]}),"instanceName":"9"});
            var Q59;
            Q59=makeQuery(id+"F8.opPattern","COPY",BODY,{"derivedFrom":makeQuery(id+"F7.opExtrude","SWEPT_BODY",BODY,{"disambiguationData":[OSD([sQuery(id+"F6.wireOp",EDGE,"E9"),sQuery(id+"F6.wireOp",EDGE,"E10"),sQuery(id+"F6.wireOp",EDGE,"E19"),sQuery(id+"F6.wireOp",EDGE,"E20")])]}),"instanceName":"9"});
            var Q60;
            Q60=makeQuery(id+"F1.opRevolve","SWEPT_BODY",BODY,{"disambiguationData":[OSD([sQuery(id+"F0.wireOp",EDGE,"E0"),sQuery(id+"F0.wireOp",EDGE,"E1"),sQuery(id+"F0.wireOp",EDGE,"E2"),sQuery(id+"F0.wireOp",EDGE,"E3"),sQuery(id+"F0.wireOp",EDGE,"E4")])]});
            booleanBodies(context, id + "F9", {"operationType" : BooleanOperationType.SUBTRACTION, "tools" : qUnion([Q0, Q1, Q2, Q3, Q4, Q5, Q6, Q7, Q8, Q9, Q10, Q11, Q12, Q13, Q14, Q15, Q16, Q17, Q18, Q19, Q20, Q21, Q22, Q23, Q24, Q25, Q26, Q27, Q28, Q29, Q30, Q31, Q32, Q33, Q34, Q35, Q36, Q37, Q38, Q39, Q40, Q41, Q42, Q43, Q44, Q45, Q46, Q47, Q48, Q49, Q50, Q51, Q52, Q53, Q54, Q55, Q56, Q57, Q58, Q59]), "targets" : qUnion([Q60])});
        }
        {
            var Q0;
            Q0=makeQuery(id+"F1.opRevolve","SWEPT_FACE",FACE,{"disambiguationData":[OSD([sQuery(id+"F0.wireOp",EDGE,"E1")])]});
            var sketch = newSketch(context, id + "F10", { "sketchPlane" : qUnion([Q0])});
            skCircle(sketch, "E23", {"center": v(-10.16, -10.16) * mm, "radius": 3.18 * mm});
            skCircle(sketch, "E24", {"center": v(-10.16, 10.16) * mm, "radius": 3.18 * mm});
            skCircle(sketch, "E25", {"center": v(10.16, -10.16) * mm, "radius": 3.18 * mm});
            skCircle(sketch, "E26", {"center": v(10.16, 10.16) * mm, "radius": 3.18 * mm});
            skSolve(sketch);
        }
        {
            var Q0;
            {Q0=qUnion([makeQuery(id+"F10.imprint","IMPRINT",FACE,{"disambiguationData":[TD([[makeQuery(id+"F10.imprint","IMPRINT",EDGE,{"derivedFrom":sQuery(id+"F10.wireOp",EDGE,"E23")}),1.0]])]}),makeQuery(id+"F10.imprint","IMPRINT",FACE,{"disambiguationData":[TD([[makeQuery(id+"F10.imprint","IMPRINT",EDGE,{"derivedFrom":sQuery(id+"F10.wireOp",EDGE,"E24")}),1.0]])]}),makeQuery(id+"F10.imprint","IMPRINT",FACE,{"disambiguationData":[TD([[makeQuery(id+"F10.imprint","IMPRINT",EDGE,{"derivedFrom":sQuery(id+"F10.wireOp",EDGE,"E25")}),1.0]])]}),makeQuery(id+"F10.imprint","IMPRINT",FACE,{"disambiguationData":[TD([[makeQuery(id+"F10.imprint","IMPRINT",EDGE,{"derivedFrom":sQuery(id+"F10.wireOp",EDGE,"E26")}),1.0]])]})]);}
            extrude(context, id + "F11", {"entities" : qUnion([Q0]), "operationType" : NewBodyOperationType.REMOVE, "endBound" : BoundingType.THROUGH_ALL, "oppositeDirection" : true, "depth" : 25.4 * mm});
        }
    });
